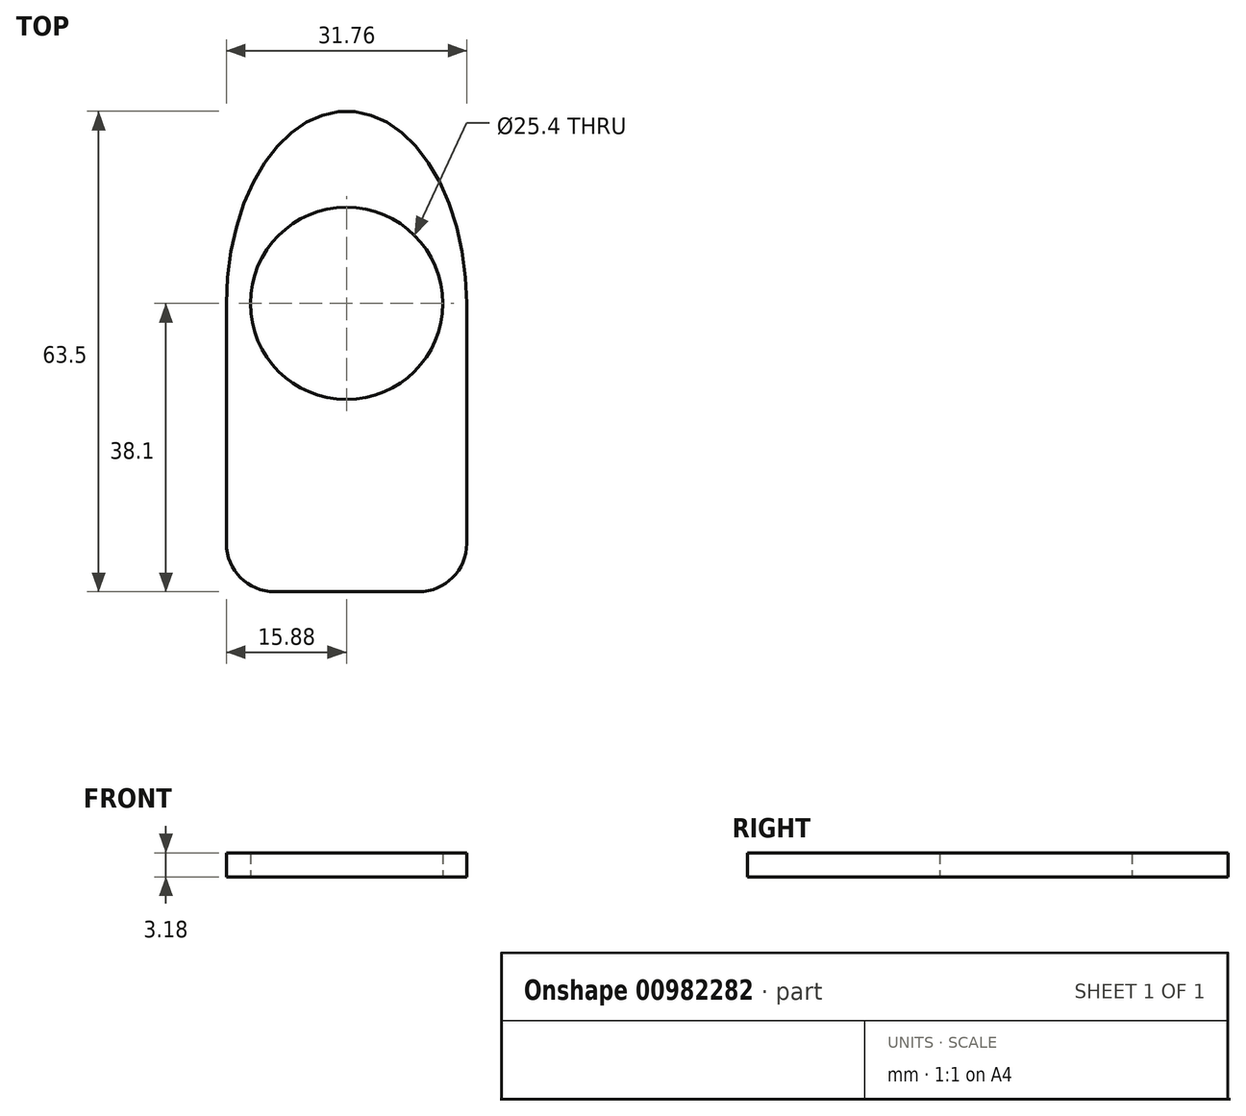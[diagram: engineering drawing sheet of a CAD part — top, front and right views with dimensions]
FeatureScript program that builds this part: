
annotation { "Feature Type Name" : "Feature", "Feature Type Description" : "" }
export const myFeature = defineFeature(function(context is Context, id is Id, definition is map)
    precondition{}
    {
        {
            var Q0;
            Q0=qCreatedBy(makeId("Top.planeOp"),FACE);
            var sketch = newSketch(context, id + "F0", { "sketchPlane" : qUnion([Q0])});
            skCircle(sketch, "E0", {"center": v(0, 0) * mm, "radius": 12.7 * mm});
            skEllipticalArc(sketch, "E1", {});
            skLineSegment(sketch, "E2.top", {"start": v(-9.52, -38.1) * mm, "end": v(9.53, -38.1) * mm});
            skLineSegment(sketch, "E2.left", {"start": v(-15.88, 0) * mm, "end": v(-15.88, -31.75) * mm});
            skLineSegment(sketch, "E2.right", {"start": v(15.88, 0) * mm, "end": v(15.88, -31.75) * mm});
            skPoint(sketch, "E3", {"position": v(0, -12.7) * mm});
            skPoint(sketch, "E4.visualSharp", {"position": v(-15.88, -38.1) * mm});
            skArc(sketch, "E4.filletArc", {"start": v(-15.88, -31.75) * mm, "mid": v(-14.02, -36.24) * mm, "end": v(-9.52, -38.1) * mm});
            skPoint(sketch, "E5.visualSharp", {"position": v(15.88, -38.1) * mm});
            skArc(sketch, "E5.filletArc", {"start": v(9.53, -38.1) * mm, "mid": v(14.02, -36.24) * mm, "end": v(15.88, -31.75) * mm});
            const initialGuessF0  = {"E1": [0, 0, 0, -1, 0.0254, 0.015875, 1.5707963267948966, 4.71238898038469]};
            skSetInitialGuess(sketch, initialGuessF0);
            skSolve(sketch);
        }
        {
            var Q0;
            Q0 = qSketchRegion(id + "F0", true);
            extrude(context, id + "F1", {"entities" : qUnion([Q0]), "depth" : 3.17 * mm, "offsetDistance" : 25.4 * mm});
        }
    });
